annotation { "Feature Type Name" : "Feature", "Feature Type Description" : "" }
export const myFeature = defineFeature(function(context is Context, id is Id, definition is map)
    precondition{}
    {
        {
            var Q0;
            Q0=qCreatedBy(makeId("Front.planeOp"),FACE);
            var sketch = newSketch(context, id + "F0", { "sketchPlane" : qUnion([Q0])});
            skLineSegment(sketch, "E0", {"start": v(-99.96, -75.7) * mm, "end": v(-99.96, -56.32) * mm});
            skLineSegment(sketch, "E1", {"start": v(-99.96, -56.32) * mm, "end": v(-75.96, -56.32) * mm});
            skLineSegment(sketch, "E2", {"start": v(-75.96, -56.32) * mm, "end": v(-75.96, -75.7) * mm});
            skLineSegment(sketch, "E3", {"start": v(-75.96, -56.32) * mm, "end": v(-75.96, -38.23) * mm});
            skLineSegment(sketch, "E4", {"start": v(-75.96, -38.23) * mm, "end": v(-37.56, -38.23) * mm});
            skLineSegment(sketch, "E5", {"start": v(-75.96, -45.62) * mm, "end": v(-38.3, -45.62) * mm});
            skLineSegment(sketch, "E6", {"start": v(-75.96, -38.23) * mm, "end": v(-75.96, -12.94) * mm});
            skLineSegment(sketch, "E7", {"start": v(-75.96, -12.94) * mm, "end": v(-68.55, -12.94) * mm});
            skLineSegment(sketch, "E8", {"start": v(-68.55, -12.94) * mm, "end": v(-68.55, 25.52) * mm});
            skLineSegment(sketch, "E9", {"start": v(-37.56, -38.23) * mm, "end": v(0, 0) * mm});
            skLineSegment(sketch, "E10", {"start": v(-38.3, -45.62) * mm, "end": v(-37.56, -38.23) * mm});
            skLineSegment(sketch, "E11", {"start": v(-38.3, -45.62) * mm, "end": v(-38.3, -75.7) * mm});
            skLineSegment(sketch, "E12", {"start": v(-68.55, -12.94) * mm, "end": v(-68.55, -19.77) * mm});
            skLineSegment(sketch, "E13", {"start": v(-68.55, -19.77) * mm, "end": v(-75.96, -19.77) * mm});
            skLineSegment(sketch, "E14", {"start": v(-68.55, -19.77) * mm, "end": v(-68.55, -38.23) * mm});
            skLineSegment(sketch, "E15", {"start": v(-68.55, 25.52) * mm, "end": v(0, 25.52) * mm});
            skLineSegment(sketch, "E16", {"start": v(-68.55, 14.35) * mm, "end": v(0, 14.35) * mm});
            skLineSegment(sketch, "E17", {"start": v(-68.55, -12.94) * mm, "end": v(-12.71, -12.94) * mm});
            skLineSegment(sketch, "E18", {"start": v(-68.55, -19.77) * mm, "end": v(-19.42, -19.77) * mm});
            skLineSegment(sketch, "E19", {"start": v(-38.3, -45.62) * mm, "end": v(-30.73, -45.62) * mm});
            skLineSegment(sketch, "E20", {"start": v(-30.73, -45.43) * mm, "end": v(-30.73, -75.9) * mm});
            skLineSegment(sketch, "E21", {"start": v(-99.96, -75.7) * mm, "end": v(-75.96, -75.7) * mm});
            skLineSegment(sketch, "E22", {"start": v(-75.96, -75.7) * mm, "end": v(-38.3, -75.7) * mm});
            skLineSegment(sketch, "E23", {"start": v(-38.3, -75.7) * mm, "end": v(-30.73, -75.9) * mm});
            skLineSegment(sketch, "E24", {"start": v(-75.96, -38.23) * mm, "end": v(-73, -38.23) * mm});
            skLineSegment(sketch, "E25.MirrorCS", {"start": v(68.55, -12.94) * mm, "end": v(68.55, -19.77) * mm});
            skLineSegment(sketch, "E26.MirrorCS", {"start": v(75.96, -38.23) * mm, "end": v(73, -38.23) * mm});
            skLineSegment(sketch, "E27.MirrorCS", {"start": v(38.3, -45.62) * mm, "end": v(37.56, -38.23) * mm});
            skLineSegment(sketch, "E28.MirrorCS", {"start": v(38.3, -75.7) * mm, "end": v(30.73, -75.9) * mm});
            skLineSegment(sketch, "E29.MirrorCS", {"start": v(38.3, -45.62) * mm, "end": v(30.73, -45.62) * mm});
            skLineSegment(sketch, "E30.MirrorCS", {"start": v(99.96, -75.7) * mm, "end": v(99.96, -56.32) * mm});
            skLineSegment(sketch, "E31.MirrorCS", {"start": v(75.96, -75.7) * mm, "end": v(38.3, -75.7) * mm});
            skLineSegment(sketch, "E32.MirrorCS", {"start": v(68.55, -19.77) * mm, "end": v(75.96, -19.77) * mm});
            skLineSegment(sketch, "E33.MirrorCS", {"start": v(68.55, -12.94) * mm, "end": v(12.71, -12.94) * mm});
            skLineSegment(sketch, "E34.MirrorCS", {"start": v(75.96, -45.62) * mm, "end": v(38.3, -45.62) * mm});
            skLineSegment(sketch, "E35.MirrorCS", {"start": v(75.96, -12.94) * mm, "end": v(68.55, -12.94) * mm});
            skLineSegment(sketch, "E36.MirrorCS", {"start": v(68.55, -19.77) * mm, "end": v(68.55, -38.23) * mm});
            skLineSegment(sketch, "E37.MirrorCS", {"start": v(99.96, -56.32) * mm, "end": v(75.96, -56.32) * mm});
            skLineSegment(sketch, "E38.MirrorCS", {"start": v(37.56, -38.23) * mm, "end": v(0, 0) * mm});
            skLineSegment(sketch, "E39.MirrorCS", {"start": v(68.55, 25.52) * mm, "end": v(0, 25.52) * mm});
            skLineSegment(sketch, "E40.MirrorCS", {"start": v(75.96, -56.32) * mm, "end": v(75.96, -38.23) * mm});
            skLineSegment(sketch, "E41.MirrorCS", {"start": v(68.55, 14.35) * mm, "end": v(0, 14.35) * mm});
            skLineSegment(sketch, "E42.MirrorCS", {"start": v(75.96, -38.23) * mm, "end": v(75.96, -12.94) * mm});
            skLineSegment(sketch, "E43.MirrorCS", {"start": v(68.55, -19.77) * mm, "end": v(19.42, -19.77) * mm});
            skLineSegment(sketch, "E44.MirrorCS", {"start": v(30.73, -45.43) * mm, "end": v(30.73, -75.9) * mm});
            skLineSegment(sketch, "E45.MirrorCS", {"start": v(99.96, -75.7) * mm, "end": v(75.96, -75.7) * mm});
            skLineSegment(sketch, "E46.MirrorCS", {"start": v(75.96, -56.32) * mm, "end": v(75.96, -75.7) * mm});
            skLineSegment(sketch, "E47.MirrorCS", {"start": v(68.55, -12.94) * mm, "end": v(68.55, 25.52) * mm});
            skLineSegment(sketch, "E48.MirrorCS", {"start": v(75.96, -38.23) * mm, "end": v(37.56, -38.23) * mm});
            skLineSegment(sketch, "E49.MirrorCS", {"start": v(38.3, -45.62) * mm, "end": v(38.3, -75.7) * mm});
            skText(sketch, "E50", { "text": "Greek Parliament", "fontName": "OpenSans-Bold.ttf"});
            const initialGuessF0  = {"E50": [-0.06855, 0.01435, 1, 0, 0.01116]};
            skSetInitialGuess(sketch, initialGuessF0);
            skSolve(sketch);
        }
        {
            var Q0;
            Q0 = qSketchRegion(id + "F0", true);
            var Q1;
            {var subQ5=sQuery(id+"F0.wireOp",EDGE,"E50.sketch_text.stroke-141");Q1=makeQuery(id+"F0.imprint","IMPRINT",FACE,{"disambiguationData":[TD([[makeQuery(id+"F0.imprint","IMPRINT",EDGE,{"derivedFrom":subQ5}),-1.0]])]});}
            var Q2;
            Q2=makeQuery(id+"F0.imprint","IMPRINT",FACE,{"disambiguationData":[TD([[makeQuery(id+"F0.imprint","IMPRINT",EDGE,{"derivedFrom":sQuery(id+"F0.wireOp",EDGE,"E25.MirrorCS")}),1.0]])]});
            var Q3;
            {var subQ0=sQuery(id+"F0.wireOp",EDGE,"E50.sketch_text.stroke-180");Q3=makeQuery(id+"F0.imprint","IMPRINT",FACE,{"disambiguationData":[TD([[makeQuery(id+"F0.imprint","IMPRINT",EDGE,{"derivedFrom":subQ0}),1.0]])]});}
            var Q4;
            {var subQ0=sQuery(id+"F0.wireOp",EDGE,"E28.MirrorCS");Q4=makeQuery(id+"F0.imprint","IMPRINT",FACE,{"disambiguationData":[TD([[makeQuery(id+"F0.imprint","IMPRINT",EDGE,{"derivedFrom":subQ0}),-1.0]])]});}
            var Q5;
            Q5=makeQuery(id+"F0.imprint","IMPRINT",FACE,{"disambiguationData":[TD([[makeQuery(id+"F0.imprint","IMPRINT",EDGE,{"derivedFrom":sQuery(id+"F0.wireOp",EDGE,"E50.sketch_text.stroke-150")}),-1.0]])]});
            var Q6;
            Q6=makeQuery(id+"F0.imprint","IMPRINT",FACE,{"disambiguationData":[TD([[makeQuery(id+"F0.imprint","IMPRINT",EDGE,{"derivedFrom":sQuery(id+"F0.wireOp",EDGE,"E50.sketch_text.stroke-0")}),1.0]])]});
            var Q7;
            Q7=makeQuery(id+"F0.imprint","IMPRINT",FACE,{"disambiguationData":[TD([[makeQuery(id+"F0.imprint","IMPRINT",EDGE,{"derivedFrom":sQuery(id+"F0.wireOp",EDGE,"E50.sketch_text.stroke-19")}),-1.0]])]});
            var Q8;
            Q8=makeQuery(id+"F0.imprint","IMPRINT",FACE,{"disambiguationData":[TD([[makeQuery(id+"F0.imprint","IMPRINT",EDGE,{"derivedFrom":sQuery(id+"F0.wireOp",EDGE,"E31.MirrorCS")}),-1.0]])]});
            var Q9;
            {var subQ1=sQuery(id+"F0.wireOp",EDGE,"E32.MirrorCS");Q9=makeQuery(id+"F0.imprint","IMPRINT",FACE,{"disambiguationData":[TD([[makeQuery(id+"F0.imprint","IMPRINT",EDGE,{"derivedFrom":subQ1}),-1.0]])]});}
            var Q10;
            {var subQ2=sQuery(id+"F0.wireOp",EDGE,"E50.sketch_text.stroke-201");Q10=makeQuery(id+"F0.imprint","IMPRINT",FACE,{"disambiguationData":[TD([[makeQuery(id+"F0.imprint","IMPRINT",EDGE,{"derivedFrom":subQ2}),1.0]])]});}
            var Q11;
            Q11=makeQuery(id+"F0.imprint","IMPRINT",FACE,{"disambiguationData":[TD([[makeQuery(id+"F0.imprint","IMPRINT",EDGE,{"derivedFrom":sQuery(id+"F0.wireOp",EDGE,"E50.sketch_text.stroke-207")}),-1.0]])]});
            var Q12;
            Q12=makeQuery(id+"F0.imprint","IMPRINT",FACE,{"disambiguationData":[TD([[makeQuery(id+"F0.imprint","IMPRINT",EDGE,{"derivedFrom":sQuery(id+"F0.wireOp",EDGE,"E50.sketch_text.stroke-128")}),-1.0]])]});
            var Q13;
            Q13=makeQuery(id+"F0.imprint","IMPRINT",FACE,{"disambiguationData":[TD([[makeQuery(id+"F0.imprint","IMPRINT",EDGE,{"derivedFrom":sQuery(id+"F0.wireOp",EDGE,"E30.MirrorCS")}),1.0]])]});
            var Q14;
            {var subQ37=sQuery(id+"F0.wireOp",EDGE,"E17");Q14=makeQuery(id+"F0.imprint","IMPRINT",FACE,{"disambiguationData":[TD([[makeQuery(id+"F0.imprint","IMPRINT",EDGE,{"derivedFrom":subQ37}),1.0]])]});}
            var Q15;
            Q15=makeQuery(id+"F0.imprint","IMPRINT",FACE,{"disambiguationData":[TD([[makeQuery(id+"F0.imprint","IMPRINT",EDGE,{"derivedFrom":sQuery(id+"F0.wireOp",EDGE,"E50.sketch_text.stroke-227")}),-1.0]])]});
            var Q16;
            Q16=makeQuery(id+"F0.imprint","IMPRINT",FACE,{"disambiguationData":[TD([[makeQuery(id+"F0.imprint","IMPRINT",EDGE,{"derivedFrom":sQuery(id+"F0.wireOp",EDGE,"E50.sketch_text.stroke-72")}),1.0]])]});
            var Q17;
            {var subQ31=sQuery(id+"F0.wireOp",EDGE,"E50.sketch_text.stroke-147");Q17=makeQuery(id+"F0.imprint","IMPRINT",FACE,{"disambiguationData":[TD([[makeQuery(id+"F0.imprint","IMPRINT",EDGE,{"derivedFrom":subQ31}),1.0]])]});}
            var Q18;
            {var subQ0=sQuery(id+"F0.wireOp",EDGE,"E50.sketch_text.stroke-228");Q18=makeQuery(id+"F0.imprint","IMPRINT",FACE,{"disambiguationData":[TD([[makeQuery(id+"F0.imprint","IMPRINT",EDGE,{"derivedFrom":subQ0}),1.0]])]});}
            var Q19;
            {var subQ5=sQuery(id+"F0.wireOp",EDGE,"E50.sketch_text.stroke-3");Q19=makeQuery(id+"F0.imprint","IMPRINT",FACE,{"disambiguationData":[TD([[makeQuery(id+"F0.imprint","IMPRINT",EDGE,{"derivedFrom":subQ5}),-1.0]])]});}
            var Q20;
            {var subQ0=sQuery(id+"F0.wireOp",EDGE,"E36.MirrorCS");Q20=makeQuery(id+"F0.imprint","IMPRINT",FACE,{"disambiguationData":[TD([[makeQuery(id+"F0.imprint","IMPRINT",EDGE,{"derivedFrom":subQ0}),-1.0]])]});}
            var Q21;
            {var subQ5=sQuery(id+"F0.wireOp",EDGE,"E27.MirrorCS");Q21=makeQuery(id+"F0.imprint","IMPRINT",FACE,{"disambiguationData":[TD([[makeQuery(id+"F0.imprint","IMPRINT",EDGE,{"derivedFrom":subQ5}),-1.0]])]});}
            var Q22;
            Q22=makeQuery(id+"F0.imprint","IMPRINT",FACE,{"disambiguationData":[TD([[makeQuery(id+"F0.imprint","IMPRINT",EDGE,{"derivedFrom":sQuery(id+"F0.wireOp",EDGE,"E50.sketch_text.stroke-154")}),-1.0]])]});
            var Q23;
            Q23=makeQuery(id+"F0.imprint","IMPRINT",FACE,{"disambiguationData":[TD([[makeQuery(id+"F0.imprint","IMPRINT",EDGE,{"derivedFrom":sQuery(id+"F0.wireOp",EDGE,"E0")}),-1.0]])]});
            var Q24;
            {var subQ1=sQuery(id+"F0.wireOp",EDGE,"E2");Q24=makeQuery(id+"F0.imprint","IMPRINT",FACE,{"disambiguationData":[TD([[makeQuery(id+"F0.imprint","IMPRINT",EDGE,{"derivedFrom":subQ1}),1.0]])]});}
            var Q25;
            Q25=makeQuery(id+"F0.imprint","IMPRINT",FACE,{"disambiguationData":[TD([[makeQuery(id+"F0.imprint","IMPRINT",EDGE,{"derivedFrom":sQuery(id+"F0.wireOp",EDGE,"E50.sketch_text.stroke-0")}),-1.0]])]});
            var Q26;
            Q26=makeQuery(id+"F0.imprint","IMPRINT",FACE,{"disambiguationData":[TD([[makeQuery(id+"F0.imprint","IMPRINT",EDGE,{"derivedFrom":sQuery(id+"F0.wireOp",EDGE,"E25.MirrorCS")}),-1.0]])]});
            var Q27;
            Q27=makeQuery(id+"F0.imprint","IMPRINT",FACE,{"disambiguationData":[TD([[makeQuery(id+"F0.imprint","IMPRINT",EDGE,{"derivedFrom":sQuery(id+"F0.wireOp",EDGE,"E50.sketch_text.stroke-179")}),-1.0]])]});
            var Q28;
            Q28 = qSketchRegion(id + "Fgkdy6W4aOlHNqu_0", true);
            var Q29;
            Q29=makeQuery(id+"F0.imprint","IMPRINT",FACE,{"disambiguationData":[TD([[makeQuery(id+"F0.imprint","IMPRINT",EDGE,{"derivedFrom":sQuery(id+"F0.wireOp",EDGE,"E50.sketch_text.stroke-103")}),-1.0]])]});
            var Q30;
            {var subQ5=sQuery(id+"F0.wireOp",EDGE,"E50.sketch_text.stroke-71");Q30=makeQuery(id+"F0.imprint","IMPRINT",FACE,{"disambiguationData":[TD([[makeQuery(id+"F0.imprint","IMPRINT",EDGE,{"derivedFrom":subQ5}),-1.0]])]});}
            var Q31;
            Q31=makeQuery(id+"F0.imprint","IMPRINT",FACE,{"disambiguationData":[TD([[makeQuery(id+"F0.imprint","IMPRINT",EDGE,{"derivedFrom":sQuery(id+"F0.wireOp",EDGE,"E50.sketch_text.stroke-172")}),1.0]])]});
            var Q32;
            Q32=makeQuery(id+"F0.imprint","IMPRINT",FACE,{"disambiguationData":[TD([[makeQuery(id+"F0.imprint","IMPRINT",EDGE,{"derivedFrom":sQuery(id+"F0.wireOp",EDGE,"E50.sketch_text.stroke-121")}),1.0]])]});
            var Q33;
            Q33=makeQuery(id+"F0.imprint","IMPRINT",FACE,{"disambiguationData":[TD([[makeQuery(id+"F0.imprint","IMPRINT",EDGE,{"derivedFrom":sQuery(id+"F0.wireOp",EDGE,"E50.sketch_text.stroke-52")}),-1.0]])]});
            var Q34;
            {var subQ0=sQuery(id+"F0.wireOp",EDGE,"E50.sketch_text.stroke-5");Q34=makeQuery(id+"F0.imprint","IMPRINT",FACE,{"disambiguationData":[TD([[makeQuery(id+"F0.imprint","IMPRINT",EDGE,{"derivedFrom":subQ0}),1.0]])]});}
            var Q35;
            Q35=makeQuery(id+"F0.imprint","IMPRINT",FACE,{"disambiguationData":[TD([[makeQuery(id+"F0.imprint","IMPRINT",EDGE,{"derivedFrom":sQuery(id+"F0.wireOp",EDGE,"E50.sketch_text.stroke-32")}),1.0]])]});
            var Q36;
            Q36=makeQuery(id+"F0.imprint","IMPRINT",FACE,{"disambiguationData":[TD([[makeQuery(id+"F0.imprint","IMPRINT",EDGE,{"derivedFrom":sQuery(id+"F0.wireOp",EDGE,"E11")}),1.0]])]});
            var Q37;
            Q37=makeQuery(id+"F0.imprint","IMPRINT",FACE,{"disambiguationData":[TD([[makeQuery(id+"F0.imprint","IMPRINT",EDGE,{"derivedFrom":sQuery(id+"F0.wireOp",EDGE,"E50.sketch_text.stroke-72")}),-1.0]])]});
            var Q38;
            {var subQ0=sQuery(id+"F0.wireOp",EDGE,"E13");Q38=makeQuery(id+"F0.imprint","IMPRINT",FACE,{"disambiguationData":[TD([[makeQuery(id+"F0.imprint","IMPRINT",EDGE,{"derivedFrom":subQ0}),1.0]])]});}
            var Q39;
            {var subQ5=sQuery(id+"F0.wireOp",EDGE,"E50.sketch_text.stroke-51");Q39=makeQuery(id+"F0.imprint","IMPRINT",FACE,{"disambiguationData":[TD([[makeQuery(id+"F0.imprint","IMPRINT",EDGE,{"derivedFrom":subQ5}),-1.0]])]});}
            var Q40;
            Q40=makeQuery(id+"F0.imprint","IMPRINT",FACE,{"disambiguationData":[TD([[makeQuery(id+"F0.imprint","IMPRINT",EDGE,{"derivedFrom":sQuery(id+"F0.wireOp",EDGE,"E50.sketch_text.stroke-32")}),-1.0]])]});
            var Q41;
            Q41=makeQuery(id+"F0.imprint","IMPRINT",FACE,{"disambiguationData":[TD([[makeQuery(id+"F0.imprint","IMPRINT",EDGE,{"derivedFrom":sQuery(id+"F0.wireOp",EDGE,"E50.sketch_text.stroke-244")}),-1.0]])]});
            var Q42;
            Q42=makeQuery(id+"F0.imprint","IMPRINT",FACE,{"disambiguationData":[TD([[makeQuery(id+"F0.imprint","IMPRINT",EDGE,{"derivedFrom":sQuery(id+"F0.wireOp",EDGE,"E50.sketch_text.stroke-207")}),1.0]])]});
            var Q43;
            Q43=makeQuery(id+"F0.imprint","IMPRINT",FACE,{"disambiguationData":[TD([[makeQuery(id+"F0.imprint","IMPRINT",EDGE,{"derivedFrom":sQuery(id+"F0.wireOp",EDGE,"E50.sketch_text.stroke-87")}),1.0]])]});
            var Q44;
            Q44=makeQuery(id+"F0.imprint","IMPRINT",FACE,{"disambiguationData":[TD([[makeQuery(id+"F0.imprint","IMPRINT",EDGE,{"derivedFrom":sQuery(id+"F0.wireOp",EDGE,"E50.sketch_text.stroke-87")}),-1.0]])]});
            var Q45;
            {var subQ0=sQuery(id+"F0.wireOp",EDGE,"E50.sketch_text.stroke-78");Q45=makeQuery(id+"F0.imprint","IMPRINT",FACE,{"disambiguationData":[TD([[makeQuery(id+"F0.imprint","IMPRINT",EDGE,{"derivedFrom":subQ0}),1.0]])]});}
            var Q46;
            {var subQ0=sQuery(id+"F0.wireOp",EDGE,"E5");Q46=makeQuery(id+"F0.imprint","IMPRINT",FACE,{"disambiguationData":[TD([[makeQuery(id+"F0.imprint","IMPRINT",EDGE,{"derivedFrom":subQ0}),1.0]])]});}
            var Q47;
            Q47=makeQuery(id+"F0.imprint","IMPRINT",FACE,{"disambiguationData":[TD([[makeQuery(id+"F0.imprint","IMPRINT",EDGE,{"derivedFrom":sQuery(id+"F0.wireOp",EDGE,"E50.sketch_text.stroke-52")}),1.0]])]});
            var Q48;
            {var subQ5=sQuery(id+"F0.wireOp",EDGE,"E50.sketch_text.stroke-226");Q48=makeQuery(id+"F0.imprint","IMPRINT",FACE,{"disambiguationData":[TD([[makeQuery(id+"F0.imprint","IMPRINT",EDGE,{"derivedFrom":subQ5}),-1.0]])]});}
            var Q49;
            Q49=makeQuery(id+"F0.imprint","IMPRINT",FACE,{"disambiguationData":[TD([[makeQuery(id+"F0.imprint","IMPRINT",EDGE,{"derivedFrom":sQuery(id+"F0.wireOp",EDGE,"E12")}),1.0]])]});
            var Q50;
            {var subQ3=sQuery(id+"F0.wireOp",EDGE,"E14");Q50=makeQuery(id+"F0.imprint","IMPRINT",FACE,{"disambiguationData":[TD([[makeQuery(id+"F0.imprint","IMPRINT",EDGE,{"derivedFrom":subQ3}),1.0]])]});}
            var Q51;
            {var subQ0=sQuery(id+"F0.wireOp",EDGE,"E7");Q51=makeQuery(id+"F0.imprint","IMPRINT",FACE,{"disambiguationData":[TD([[makeQuery(id+"F0.imprint","IMPRINT",EDGE,{"derivedFrom":subQ0}),-1.0]])]});}
            var Q52;
            Q52=makeQuery(id+"Fgkdy6W4aOlHNqu_0.imprint","IMPRINT",FACE,{"disambiguationData":[TD([[makeQuery(id+"Fgkdy6W4aOlHNqu_0.imprint","IMPRINT",EDGE,{"derivedFrom":sQuery(id+"Fgkdy6W4aOlHNqu_0.wireOp",EDGE,"5e87d690-c448-4643-8d06-18971623fd7b.sketch_text.stroke-154")}),-1.0]])]});
            var Q53;
            Q53=makeQuery(id+"Fgkdy6W4aOlHNqu_0.imprint","IMPRINT",FACE,{"disambiguationData":[TD([[makeQuery(id+"Fgkdy6W4aOlHNqu_0.imprint","IMPRINT",EDGE,{"derivedFrom":sQuery(id+"Fgkdy6W4aOlHNqu_0.wireOp",EDGE,"5e87d690-c448-4643-8d06-18971623fd7b.sketch_text.stroke-103")}),-1.0]])]});
            var Q54;
            Q54=makeQuery(id+"Fgkdy6W4aOlHNqu_0.imprint","IMPRINT",FACE,{"disambiguationData":[TD([[makeQuery(id+"Fgkdy6W4aOlHNqu_0.imprint","IMPRINT",EDGE,{"derivedFrom":sQuery(id+"Fgkdy6W4aOlHNqu_0.wireOp",EDGE,"5e87d690-c448-4643-8d06-18971623fd7b.sketch_text.stroke-207")}),-1.0]])]});
            var Q55;
            Q55=makeQuery(id+"Fgkdy6W4aOlHNqu_0.imprint","IMPRINT",FACE,{"disambiguationData":[TD([[makeQuery(id+"Fgkdy6W4aOlHNqu_0.imprint","IMPRINT",EDGE,{"derivedFrom":sQuery(id+"Fgkdy6W4aOlHNqu_0.wireOp",EDGE,"5e87d690-c448-4643-8d06-18971623fd7b.sketch_text.stroke-87")}),1.0]])]});
            var Q56;
            Q56=makeQuery(id+"Fgkdy6W4aOlHNqu_0.imprint","IMPRINT",FACE,{"disambiguationData":[TD([[makeQuery(id+"Fgkdy6W4aOlHNqu_0.imprint","IMPRINT",EDGE,{"derivedFrom":sQuery(id+"Fgkdy6W4aOlHNqu_0.wireOp",EDGE,"5e87d690-c448-4643-8d06-18971623fd7b.sketch_text.stroke-87")}),-1.0]])]});
            var Q57;
            Q57=makeQuery(id+"Fgkdy6W4aOlHNqu_0.imprint","IMPRINT",FACE,{"disambiguationData":[TD([[makeQuery(id+"Fgkdy6W4aOlHNqu_0.imprint","IMPRINT",EDGE,{"derivedFrom":sQuery(id+"Fgkdy6W4aOlHNqu_0.wireOp",EDGE,"5e87d690-c448-4643-8d06-18971623fd7b.sketch_text.stroke-244")}),-1.0]])]});
            var Q58;
            Q58=makeQuery(id+"Fgkdy6W4aOlHNqu_0.imprint","IMPRINT",FACE,{"disambiguationData":[TD([[makeQuery(id+"Fgkdy6W4aOlHNqu_0.imprint","IMPRINT",EDGE,{"derivedFrom":sQuery(id+"Fgkdy6W4aOlHNqu_0.wireOp",EDGE,"5e87d690-c448-4643-8d06-18971623fd7b.sketch_text.stroke-227")}),-1.0]])]});
            var Q59;
            Q59=makeQuery(id+"Fgkdy6W4aOlHNqu_0.imprint","IMPRINT",FACE,{"disambiguationData":[TD([[makeQuery(id+"Fgkdy6W4aOlHNqu_0.imprint","IMPRINT",EDGE,{"derivedFrom":sQuery(id+"Fgkdy6W4aOlHNqu_0.wireOp",EDGE,"5e87d690-c448-4643-8d06-18971623fd7b.sketch_text.stroke-52")}),-1.0]])]});
            var Q60;
            Q60=makeQuery(id+"Fgkdy6W4aOlHNqu_0.imprint","IMPRINT",FACE,{"disambiguationData":[TD([[makeQuery(id+"Fgkdy6W4aOlHNqu_0.imprint","IMPRINT",EDGE,{"derivedFrom":sQuery(id+"Fgkdy6W4aOlHNqu_0.wireOp",EDGE,"5e87d690-c448-4643-8d06-18971623fd7b.sketch_text.stroke-32")}),-1.0]])]});
            var Q61;
            Q61=makeQuery(id+"Fgkdy6W4aOlHNqu_0.imprint","IMPRINT",FACE,{"disambiguationData":[TD([[makeQuery(id+"Fgkdy6W4aOlHNqu_0.imprint","IMPRINT",EDGE,{"derivedFrom":sQuery(id+"Fgkdy6W4aOlHNqu_0.wireOp",EDGE,"5e87d690-c448-4643-8d06-18971623fd7b.sketch_text.stroke-179")}),-1.0]])]});
            var Q62;
            Q62=makeQuery(id+"Fgkdy6W4aOlHNqu_0.imprint","IMPRINT",FACE,{"disambiguationData":[TD([[makeQuery(id+"Fgkdy6W4aOlHNqu_0.imprint","IMPRINT",EDGE,{"derivedFrom":sQuery(id+"Fgkdy6W4aOlHNqu_0.wireOp",EDGE,"5e87d690-c448-4643-8d06-18971623fd7b.sketch_text.stroke-141")}),-1.0]])]});
            var Q63;
            Q63=makeQuery(id+"Fgkdy6W4aOlHNqu_0.imprint","IMPRINT",FACE,{"disambiguationData":[TD([[makeQuery(id+"Fgkdy6W4aOlHNqu_0.imprint","IMPRINT",EDGE,{"derivedFrom":sQuery(id+"Fgkdy6W4aOlHNqu_0.wireOp",EDGE,"5e87d690-c448-4643-8d06-18971623fd7b.sketch_text.stroke-72")}),-1.0]])]});
            var Q64;
            Q64=makeQuery(id+"Fgkdy6W4aOlHNqu_0.imprint","IMPRINT",FACE,{"disambiguationData":[TD([[makeQuery(id+"Fgkdy6W4aOlHNqu_0.imprint","IMPRINT",EDGE,{"derivedFrom":sQuery(id+"Fgkdy6W4aOlHNqu_0.wireOp",EDGE,"5e87d690-c448-4643-8d06-18971623fd7b.sketch_text.stroke-0")}),-1.0]])]});
            var Q65;
            Q65=makeQuery(id+"Fgkdy6W4aOlHNqu_0.imprint","IMPRINT",FACE,{"disambiguationData":[TD([[makeQuery(id+"Fgkdy6W4aOlHNqu_0.imprint","IMPRINT",EDGE,{"derivedFrom":sQuery(id+"Fgkdy6W4aOlHNqu_0.wireOp",EDGE,"5e87d690-c448-4643-8d06-18971623fd7b.sketch_text.stroke-128")}),-1.0]])]});
            var Q66;
            Q66=makeQuery(id+"Fgkdy6W4aOlHNqu_0.imprint","IMPRINT",FACE,{"disambiguationData":[TD([[makeQuery(id+"Fgkdy6W4aOlHNqu_0.imprint","IMPRINT",EDGE,{"derivedFrom":sQuery(id+"Fgkdy6W4aOlHNqu_0.wireOp",EDGE,"5e87d690-c448-4643-8d06-18971623fd7b.sketch_text.stroke-150")}),-1.0]])]});
            var Q67;
            Q67=makeQuery(id+"Fgkdy6W4aOlHNqu_0.imprint","IMPRINT",FACE,{"disambiguationData":[TD([[makeQuery(id+"Fgkdy6W4aOlHNqu_0.imprint","IMPRINT",EDGE,{"derivedFrom":sQuery(id+"Fgkdy6W4aOlHNqu_0.wireOp",EDGE,"5e87d690-c448-4643-8d06-18971623fd7b.sketch_text.stroke-19")}),-1.0]])]});
            var Q68;
            {var subQ0=sQuery(id+"F0.wireOp",EDGE,"E50.sketch_text.stroke-7");var subQ1=sQuery(id+"F0.wireOp",EDGE,"E15");var subQ2=makeQuery(id+"F0.imprint","INTERSECT",VERTEX,{"derivedFrom":[subQ1,subQ0]});Q68=makeQuery(id+"F0.imprint","IMPRINT",FACE,{"disambiguationData":[TD([[makeQuery(id+"F0.imprint","IMPRINT",EDGE,{"disambiguationData":[TD([[subQ2,-1.0]])],"derivedFrom":subQ1}),1.0]])]});}
            var Q69;
            {var subQ0=sQuery(id+"F0.wireOp",EDGE,"E50.sketch_text.stroke-246");var subQ1=sQuery(id+"F0.wireOp",EDGE,"E41.MirrorCS");var subQ2=makeQuery(id+"F0.imprint","INTERSECT",VERTEX,{"derivedFrom":[subQ1,subQ0]});Q69=makeQuery(id+"F0.imprint","IMPRINT",FACE,{"disambiguationData":[TD([[makeQuery(id+"F0.imprint","IMPRINT",EDGE,{"disambiguationData":[TD([[subQ2,-1.0]])],"derivedFrom":subQ1}),1.0]])]});}
            var Q70;
            {var subQ5=sQuery(id+"F0.wireOp",EDGE,"E50.sketch_text.stroke-143");Q70=makeQuery(id+"F0.imprint","IMPRINT",FACE,{"disambiguationData":[TD([[makeQuery(id+"F0.imprint","IMPRINT",EDGE,{"derivedFrom":subQ5}),-1.0]])]});}
            var Q71;
            {var subQ5=sQuery(id+"F0.wireOp",EDGE,"E50.sketch_text.stroke-83");Q71=makeQuery(id+"F0.imprint","IMPRINT",FACE,{"disambiguationData":[TD([[makeQuery(id+"F0.imprint","IMPRINT",EDGE,{"derivedFrom":subQ5}),-1.0]])]});}
            var Q72;
            {var subQ0=sQuery(id+"F0.wireOp",EDGE,"E50.sketch_text.stroke-154");Q72=makeQuery(id+"F0.imprint","IMPRINT",FACE,{"disambiguationData":[TD([[makeQuery(id+"F0.imprint","IMPRINT",EDGE,{"derivedFrom":subQ0}),1.0]])]});}
            var Q73;
            {var subQ0=sQuery(id+"F0.wireOp",EDGE,"E50.sketch_text.stroke-147");Q73=makeQuery(id+"F0.imprint","IMPRINT",FACE,{"disambiguationData":[TD([[makeQuery(id+"F0.imprint","IMPRINT",EDGE,{"derivedFrom":subQ0}),-1.0]])]});}
            var Q74;
            {var subQ0=sQuery(id+"F0.wireOp",EDGE,"E50.sketch_text.stroke-107");var subQ1=sQuery(id+"F0.wireOp",EDGE,"E16");var subQ2=makeQuery(id+"F0.imprint","INTERSECT",VERTEX,{"derivedFrom":[subQ1,subQ0]});Q74=makeQuery(id+"F0.imprint","IMPRINT",FACE,{"disambiguationData":[TD([[makeQuery(id+"F0.imprint","IMPRINT",EDGE,{"disambiguationData":[TD([[subQ2,-1.0]])],"derivedFrom":subQ1}),-1.0]])]});}
            var Q75;
            {var subQ0=sQuery(id+"F0.wireOp",EDGE,"E50.sketch_text.stroke-103");Q75=makeQuery(id+"F0.imprint","IMPRINT",FACE,{"disambiguationData":[TD([[makeQuery(id+"F0.imprint","IMPRINT",EDGE,{"derivedFrom":subQ0}),1.0]])]});}
            var Q76;
            {var subQ0=sQuery(id+"F0.wireOp",EDGE,"E50.sketch_text.stroke-157");var subQ1=sQuery(id+"F0.wireOp",EDGE,"E41.MirrorCS");var subQ2=makeQuery(id+"F0.imprint","INTERSECT",VERTEX,{"derivedFrom":[subQ1,subQ0]});Q76=makeQuery(id+"F0.imprint","IMPRINT",FACE,{"disambiguationData":[TD([[makeQuery(id+"F0.imprint","IMPRINT",EDGE,{"disambiguationData":[TD([[subQ2,-1.0]])],"derivedFrom":subQ1}),1.0]])]});}
            var Q77;
            {var subQ0=sQuery(id+"F0.wireOp",EDGE,"E50.sketch_text.stroke-146");var subQ1=sQuery(id+"F0.wireOp",EDGE,"E39.MirrorCS");var subQ2=makeQuery(id+"F0.imprint","INTERSECT",VERTEX,{"derivedFrom":[subQ1,subQ0]});Q77=makeQuery(id+"F0.imprint","IMPRINT",FACE,{"disambiguationData":[TD([[makeQuery(id+"F0.imprint","IMPRINT",EDGE,{"disambiguationData":[TD([[subQ2,-1.0]])],"derivedFrom":subQ1}),-1.0]])]});}
            var Q78;
            Q78=makeQuery(id+"Fgkdy6W4aOlHNqu_0.imprint","IMPRINT",FACE,{"disambiguationData":[TD([[makeQuery(id+"Fgkdy6W4aOlHNqu_0.imprint","IMPRINT",EDGE,{"derivedFrom":sQuery(id+"Fgkdy6W4aOlHNqu_0.wireOp",EDGE,"5e87d690-c448-4643-8d06-18971623fd7b.sketch_text.stroke-207")}),1.0]])]});
            var Q79;
            Q79=makeQuery(id+"Fgkdy6W4aOlHNqu_0.imprint","IMPRINT",FACE,{"disambiguationData":[TD([[makeQuery(id+"Fgkdy6W4aOlHNqu_0.imprint","IMPRINT",EDGE,{"derivedFrom":sQuery(id+"Fgkdy6W4aOlHNqu_0.wireOp",EDGE,"5e87d690-c448-4643-8d06-18971623fd7b.sketch_text.stroke-121")}),1.0]])]});
            var Q80;
            Q80=makeQuery(id+"Fgkdy6W4aOlHNqu_0.imprint","IMPRINT",FACE,{"disambiguationData":[TD([[makeQuery(id+"Fgkdy6W4aOlHNqu_0.imprint","IMPRINT",EDGE,{"derivedFrom":sQuery(id+"Fgkdy6W4aOlHNqu_0.wireOp",EDGE,"5e87d690-c448-4643-8d06-18971623fd7b.sketch_text.stroke-172")}),1.0]])]});
            var Q81;
            Q81=makeQuery(id+"Fgkdy6W4aOlHNqu_0.imprint","IMPRINT",FACE,{"disambiguationData":[TD([[makeQuery(id+"Fgkdy6W4aOlHNqu_0.imprint","IMPRINT",EDGE,{"derivedFrom":sQuery(id+"Fgkdy6W4aOlHNqu_0.wireOp",EDGE,"5e87d690-c448-4643-8d06-18971623fd7b.sketch_text.stroke-52")}),1.0]])]});
            var Q82;
            Q82=makeQuery(id+"Fgkdy6W4aOlHNqu_0.imprint","IMPRINT",FACE,{"disambiguationData":[TD([[makeQuery(id+"Fgkdy6W4aOlHNqu_0.imprint","IMPRINT",EDGE,{"derivedFrom":sQuery(id+"Fgkdy6W4aOlHNqu_0.wireOp",EDGE,"5e87d690-c448-4643-8d06-18971623fd7b.sketch_text.stroke-32")}),1.0]])]});
            var Q83;
            Q83=makeQuery(id+"Fgkdy6W4aOlHNqu_0.imprint","IMPRINT",FACE,{"disambiguationData":[TD([[makeQuery(id+"Fgkdy6W4aOlHNqu_0.imprint","IMPRINT",EDGE,{"derivedFrom":sQuery(id+"Fgkdy6W4aOlHNqu_0.wireOp",EDGE,"5e87d690-c448-4643-8d06-18971623fd7b.sketch_text.stroke-145")}),-1.0]])]});
            extrude(context, id + "F1", {"entities" : qUnion([Q0, Q1, Q2, Q3, Q4, Q5, Q6, Q7, Q8, Q9, Q10, Q11, Q12, Q13, Q14, Q15, Q16, Q17, Q18, Q19, Q20, Q21, Q22, Q23, Q24, Q25, Q26, Q27, Q28, Q29, Q30, Q31, Q32, Q33, Q34, Q35, Q36, Q37, Q38, Q39, Q40, Q41, Q42, Q43, Q44, Q45, Q46, Q47, Q48, Q49, Q50, Q51, Q52, Q53, Q54, Q55, Q56, Q57, Q58, Q59, Q60, Q61, Q62, Q63, Q64, Q65, Q66, Q67, Q68, Q69, Q70, Q71, Q72, Q73, Q74, Q75, Q76, Q77, Q78, Q79, Q80, Q81, Q82, Q83]), "depth" : 38.6 * mm, "offsetDistance" : 25.4 * mm});
        }
    });